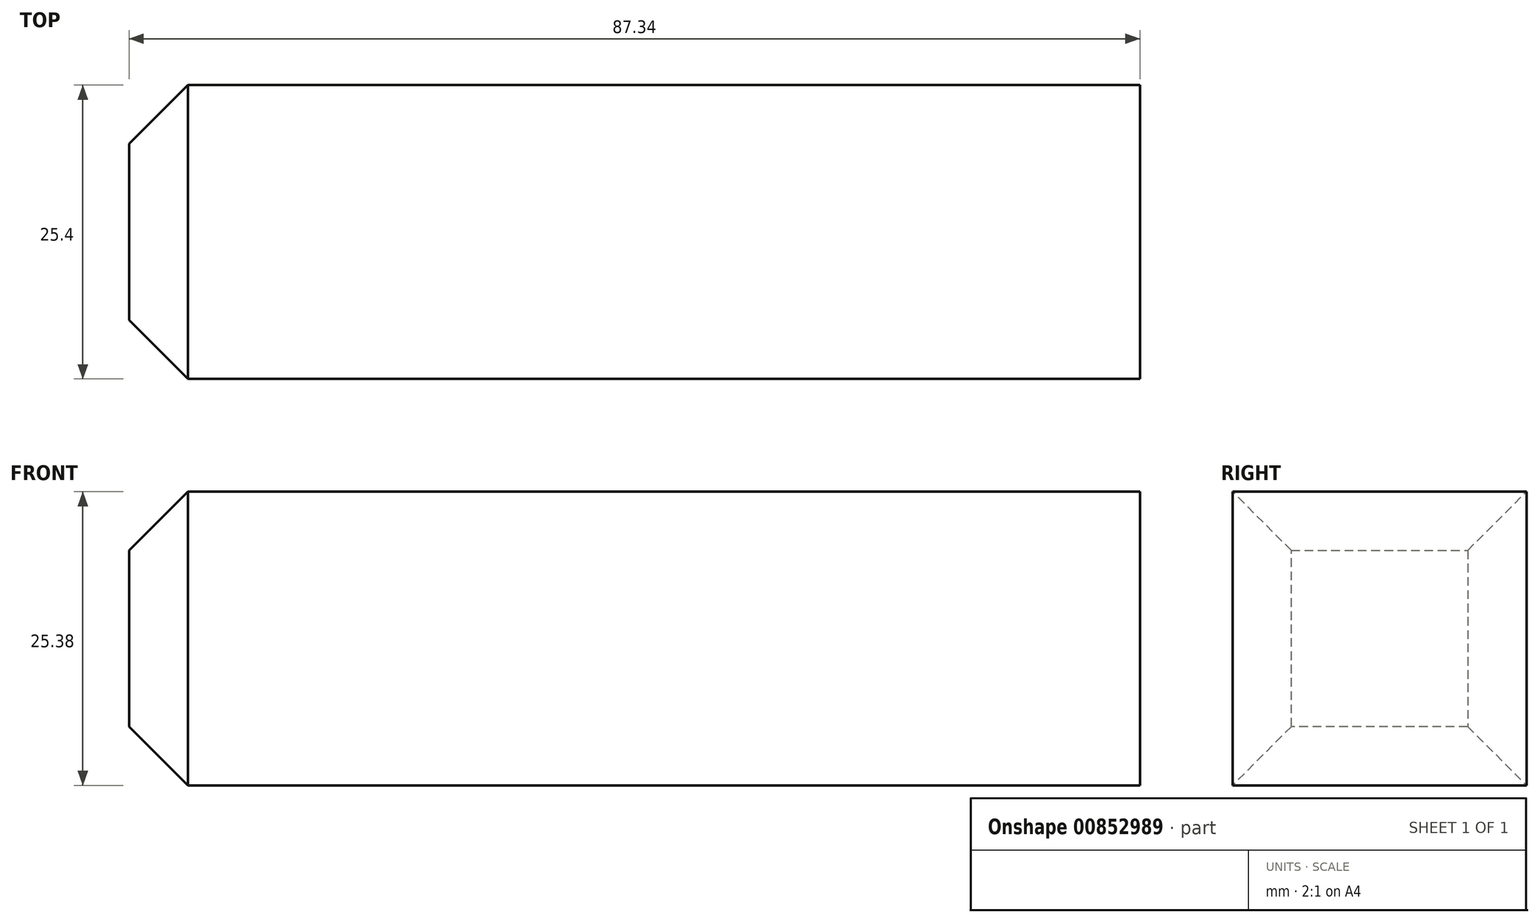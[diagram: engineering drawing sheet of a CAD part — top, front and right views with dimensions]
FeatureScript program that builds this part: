
annotation { "Feature Type Name" : "Feature", "Feature Type Description" : "" }
export const myFeature = defineFeature(function(context is Context, id is Id, definition is map)
    precondition{}
    {
        {
            var Q0;
            Q0=qCreatedBy(makeId("Front.planeOp"),FACE);
            var sketch = newSketch(context, id + "F0", { "sketchPlane" : qUnion([Q0])});
            skLineSegment(sketch, "E0.bottom", {"start": v(0, 25.38) * mm, "end": v(-87.34, 25.38) * mm});
            skLineSegment(sketch, "E0.top", {"start": v(0, 0) * mm, "end": v(-87.34, 0) * mm});
            skLineSegment(sketch, "E0.left", {"start": v(0, 25.38) * mm, "end": v(0, 0) * mm});
            skLineSegment(sketch, "E0.right", {"start": v(-87.34, 25.38) * mm, "end": v(-87.34, 0) * mm});
            skSolve(sketch);
        }
        {
            var Q0;
            Q0=makeQuery(id+"F0.imprint","IMPRINT",FACE,{"disambiguationData":[TD([[makeQuery(id+"F0.imprint","IMPRINT",EDGE,{"derivedFrom":sQuery(id+"F0.wireOp",EDGE,"E0.bottom")}),1.0]])]});
            extrude(context, id + "F1", {"entities" : qUnion([Q0]), "depth" : 25.4 * mm, "offsetDistance" : 25.4 * mm});
        }
        {
            var Q0;
            Q0=makeQuery(id+"F1.opExtrude","SWEPT_FACE",FACE,{"disambiguationData":[OSD([sQuery(id+"F0.wireOp",EDGE,"E0.right")])]});
            chamfer(context, id + "F2", {"entities" : qUnion([Q0]), "width" : 5.08 * mm, "tangentPropagation" : true});
        }
    });
